# Revit family: TataSteel_Lintels_CN102
name_source: partatom
category: Generic Models
revit_build: Autodesk Revit 2015 (Build: 20140606_1530(x64)
units: mm (PartAtom-declared; Revit-internal decimal feet)

## types (1)
- TataSteel_Lintels_CN102
    AllowableLoadLimiting = 7 mm  [stored 0.0229659 ft]
    AssetType = FIXED
    BIMObjectName = TataSteel_Lintel_CN102_1200
    BIMobject category = Beams & Lintels
    CharacteristicDeflectionUnderLoad = 0 mm  [stored 0 ft]
    CharacteristicResistanceToFire = 60 mm
    CharacteristicThermalConductivity = 0 mm  [stored 0 ft]
    ClearSpan = 1050 mm
    Color = Black
    Description = Extra light duty internal wall lintel
    Edition number = 1
    EndBearing = 75 mm  [stored 0.246063 ft]
    ExpectedLife = 60 yrs
    Finish = Galv and Powder coated
    FireRating = 60
    Grade = DX51
    IFC Classification = Structural Member
    IfcExportAs = IfcBeamType
    IfcExportType = LINTEL
    Installation instructions = http://catnic.com
    InstallationDate = 1900-12-31T23:59:59
    IsExternal = No
    LengthIncrement = 150mm up to 3000mm. 
300mm above 3000mm
    LintelHeight = 25 mm  [stored 0.082021 ft]
    LintelLength = 1200 mm
    LintelThickness = 1 mm  [stored 0.00328084 ft]
    LintelType = SOLID INTERNAL
    LintelWidth = 98 mm
    LoadBearing = Yes
    LoadCategory = EXTRA LIGHT DUTY
    Manufacturer = Catnic, TATA
    Manufacturer country = United Kingdom
    Manufacturer name = Tata Steel
    ManufacturerURL = www.catnic.com
    Material main = Steel
    MaxLintelLength = 1200
    MinLintelLength = 1050
    Model = TataSteel_Lintel_CN102_1200
    ModelNumber = CN102
    ModelReference = Internal Walls
    NBSDescription = Pre fabricated Steel Lintel
    NBSReference = F30 755
    Name = Lintel
    Nominal height = 0
    Nominal width = 0
    NominalLength = 1200 mm
    OmniClass Code = 23-13 21 25 11
    OmniClass Description = Lintels
    Product Guid = 262bdb60-6250-4774-b5ae-736d1b76a8b3
    Product SKU = catnic-cn92-102
    Product certification = http://catnic.com
    Product family = Lintels
    Product group = Catnic
    ProductInformation = www.catnic.com
    QR code = http://bimobject.com
    Roll = 0 mm  [stored 0 ft]
    SafeWorkingLoad = 7 mm  [stored 0.0229659 ft]
    Shape = Corrugated
    Size = 25H x98W x1200L
    Slope = 0 mm  [stored 0 ft]
    Span = 1050 mm
    Steel = Steel
    TSE_BIMObjectName = TataSteel_Lintel_CN102_1200
    TSE_Documentation = www.catnic.com
    TSE_InstallationInstructions = www.catnic.com
    TSE_ManufacturerURL = www.catnic.com
    TSE_Model = TataSteel_Lintel_CN102_1200
    TSE_ProductCertification = www.catnic.com
    TSE_QR code = <None>
    Technical description = http://catnic.com
    ThermalTransmittance = 0 mm  [stored 0 ft]
    Type Image = <None>
    UNSPSC Code = 30101704
    URL = www.catnic.com
    Uniclass 1.4 Code = L3241
    Uniclass 1.4 Description = Lintels
    Uniclass 2015 Code = Pr_20_85_48
    Uniclass 2015 Name = Lintels
    Uniclass2015 = Pr_20_85_48_11
    WallThickness = 100 mm  [stored 0.328084 ft]
    WarrantyStartDate = 1900-12-31T23:59:59
    Weight = 2 mm  [stored 0.00656168 ft]
    Weight Net (Kg) = 0
    Youtube clip = https://youtu.be
    a = 5 mm  [stored 0.0164042 ft]
    b = 10 mm  [stored 0.0328084 ft]
    b1 = 50 mm  [stored 0.164042 ft]
    b2 = 50 mm  [stored 0.164042 ft]
    c = 20 mm  [stored 0.0656168 ft]
    d = 49 mm
    r = 4 mm  [stored 0.0131234 ft]
    r1 = 5 mm  [stored 0.0164042 ft]

note: [stored X ft] marks values corroborated as IEEE doubles in the binary element streams (Revit-internal decimal feet)

## geometry (parser evidence)
native form markers: Sweep x3
no freeform markers — native parametric forms only
